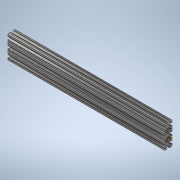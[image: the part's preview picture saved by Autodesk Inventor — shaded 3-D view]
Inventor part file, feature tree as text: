
AUTODESK INVENTOR PART (.ipt)
format: ipt  version: 2020 (Build 240168000, 168)  size: 382,464 bytes
history: native  units: in
note: dims shown in document units (in); Inventor stores cm internally (conversion verified against a paired STEP export)
features: sketch x2, extrude x1
ambient origin geometry x8: Origin, YZ Plane, XZ Plane, XY Plane, X Axis, Y Axis, Z Axis, Center Point
bodies: Solid1 (feature_tree)
feature tree (3):
  extrude  "Extrusion1"  [1 undecoded]
  sketch  "Sketch2"
  sketch  "Sketch1"  dims[d0=20.0in d1=0.0in]
note: 1 required parameter value undecoded (feature->parameter linkage not recoverable at this tier; creation-order binding heuristic only, values carry confidence <= 0.55)
